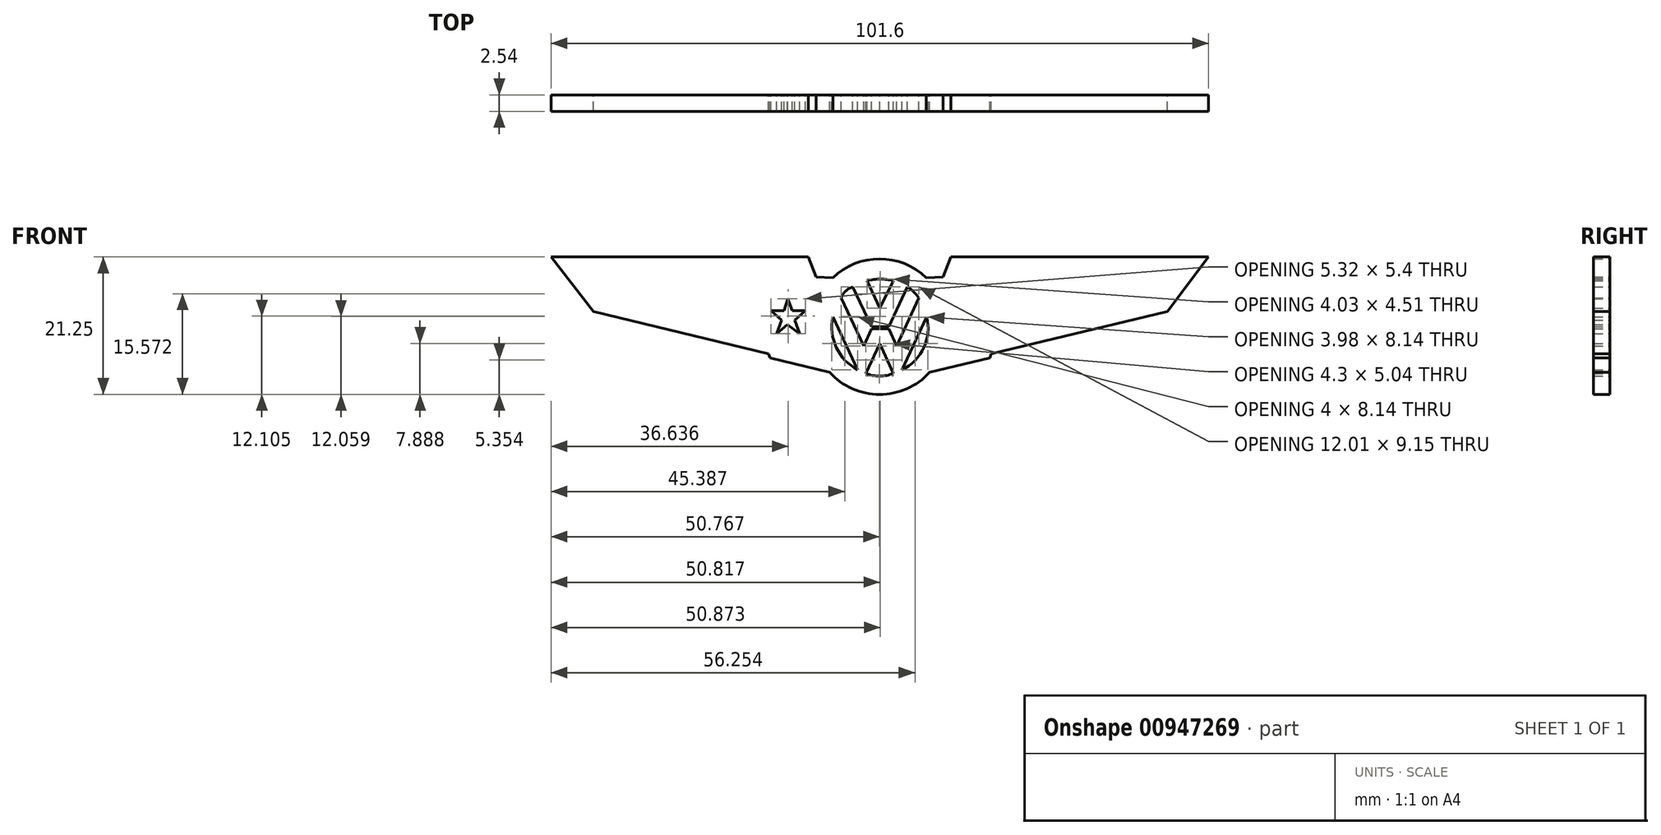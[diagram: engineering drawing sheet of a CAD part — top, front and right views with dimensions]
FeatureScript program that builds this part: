
annotation { "Feature Type Name" : "Feature", "Feature Type Description" : "" }
export const myFeature = defineFeature(function(context is Context, id is Id, definition is map)
    precondition{}
    {
        {
            var Q0;
            Q0=qCreatedBy(makeId("Front.planeOp"),FACE);
            var sketch = newSketch(context, id + "F0", { "sketchPlane" : qUnion([Q0])});
            skCircle(sketch, "E0", {"center": v(0, 0) * mm, "radius": 10.47 * mm});
            skLineSegment(sketch, "E1", {"start": v(-1.91, 7.12) * mm, "end": v(0, 2.85) * mm});
            skLineSegment(sketch, "E2", {"start": v(0, 2.85) * mm, "end": v(2.12, 7.12) * mm});
            skArc(sketch, "E3", {"start": v(2.12, 7.12) * mm, "mid": v(0.1, 7.36) * mm, "end": v(-1.91, 7.12) * mm});
            skLineSegment(sketch, "E4", {"start": v(-4.13, 6.16) * mm, "end": v(-1.23, 0) * mm});
            skLineSegment(sketch, "E5", {"start": v(-1.23, 0) * mm, "end": v(1.4, 0) * mm});
            skLineSegment(sketch, "E6", {"start": v(1.4, 0) * mm, "end": v(4.27, 6.16) * mm});
            skLineSegment(sketch, "E7", {"start": v(6.05, 4.42) * mm, "end": v(2.6, -2.98) * mm});
            skLineSegment(sketch, "E8", {"start": v(2.6, -2.98) * mm, "end": v(1.4, -0.33) * mm});
            skLineSegment(sketch, "E9", {"start": v(1.4, -0.33) * mm, "end": v(-1.23, -0.33) * mm});
            skLineSegment(sketch, "E10", {"start": v(-1.23, -0.33) * mm, "end": v(-2.47, -2.98) * mm});
            skLineSegment(sketch, "E11", {"start": v(-2.47, -2.98) * mm, "end": v(-5.96, 4.42) * mm});
            skArc(sketch, "E12", {"start": v(-4.13, 6.16) * mm, "mid": v(-5.25, 5.5) * mm, "end": v(-5.96, 4.42) * mm});
            skArc(sketch, "E13", {"start": v(6.05, 4.42) * mm, "mid": v(5.26, 5.4) * mm, "end": v(4.27, 6.16) * mm});
            skLineSegment(sketch, "E14", {"start": v(7.29, 1.49) * mm, "end": v(3.5, -6.65) * mm});
            skLineSegment(sketch, "E15", {"start": v(-7.22, 1.49) * mm, "end": v(-3.38, -6.65) * mm});
            skArc(sketch, "E16", {"start": v(-7.22, 1.49) * mm, "mid": v(-6.68, -3.23) * mm, "end": v(-3.38, -6.65) * mm});
            skArc(sketch, "E17", {"start": v(3.5, -6.65) * mm, "mid": v(6.82, -3.25) * mm, "end": v(7.29, 1.49) * mm});
            skLineSegment(sketch, "E18", {"start": v(0, -2.6) * mm, "end": v(-2.15, -7.21) * mm});
            skLineSegment(sketch, "E19", {"start": v(0, -2.6) * mm, "end": v(2.14, -7.21) * mm});
            skArc(sketch, "E20", {"start": v(-2.15, -7.21) * mm, "mid": v(0, -7.64) * mm, "end": v(2.14, -7.21) * mm});
            skLineSegment(sketch, "E21", {"start": v(-7.22, 7.58) * mm, "end": v(-21.42, 8) * mm});
            skLineSegment(sketch, "E22", {"start": v(-21.42, 8) * mm, "end": v(-16.94, -4.82) * mm});
            skLineSegment(sketch, "E23", {"start": v(-16.94, -4.82) * mm, "end": v(-7.74, -7.06) * mm});
            skLineSegment(sketch, "E24", {"start": v(-14.19, 4.33) * mm, "end": v(-13.48, 2.47) * mm});
            skLineSegment(sketch, "E25", {"start": v(-13.48, 2.47) * mm, "end": v(-11.47, 2.47) * mm});
            skLineSegment(sketch, "E26", {"start": v(-11.47, 2.47) * mm, "end": v(-13.13, 1.02) * mm});
            skLineSegment(sketch, "E27", {"start": v(-13.13, 1.02) * mm, "end": v(-12.34, -1.06) * mm});
            skLineSegment(sketch, "E28", {"start": v(-12.34, -1.06) * mm, "end": v(-14.25, 0.34) * mm});
            skLineSegment(sketch, "E29", {"start": v(-14.25, 0.34) * mm, "end": v(-15.9, -1.06) * mm});
            skLineSegment(sketch, "E30", {"start": v(-15.9, -1.06) * mm, "end": v(-15.13, 1.02) * mm});
            skLineSegment(sketch, "E31", {"start": v(-15.13, 1.02) * mm, "end": v(-16.8, 2.47) * mm});
            skLineSegment(sketch, "E32", {"start": v(-16.8, 2.47) * mm, "end": v(-14.77, 2.47) * mm});
            skLineSegment(sketch, "E33", {"start": v(-14.77, 2.47) * mm, "end": v(-14.19, 4.33) * mm});
            skLineSegment(sketch, "E34", {"start": v(7.22, 7.58) * mm, "end": v(21.52, 8) * mm});
            skLineSegment(sketch, "E35", {"start": v(21.52, 8) * mm, "end": v(17.04, -4.82) * mm});
            skLineSegment(sketch, "E36", {"start": v(17.04, -4.82) * mm, "end": v(7.74, -7.06) * mm});
            skLineSegment(sketch, "E37", {"start": v(9.83, 7.66) * mm, "end": v(11, 10.78) * mm});
            skLineSegment(sketch, "E38", {"start": v(11, 10.78) * mm, "end": v(50.83, 10.78) * mm});
            skLineSegment(sketch, "E39", {"start": v(50.83, 10.78) * mm, "end": v(44.49, 2.37) * mm});
            skLineSegment(sketch, "E40", {"start": v(44.49, 2.37) * mm, "end": v(17.26, -4.2) * mm});
            skLineSegment(sketch, "E41", {"start": v(-9.82, 7.66) * mm, "end": v(-11.01, 10.78) * mm});
            skLineSegment(sketch, "E42", {"start": v(-11.01, 10.78) * mm, "end": v(-50.77, 10.78) * mm});
            skLineSegment(sketch, "E43", {"start": v(-50.77, 10.78) * mm, "end": v(-44.23, 2.37) * mm});
            skLineSegment(sketch, "E44", {"start": v(-44.23, 2.37) * mm, "end": v(-17.16, -4.2) * mm});
            skSolve(sketch);
        }
        {
            var Q0;
            Q0 = qSketchRegion(id + "F0", true);
            extrude(context, id + "F1", {"entities" : qUnion([Q0]), "depth" : 2.54 * mm, "offsetDistance" : 25.4 * mm});
        }
    });
